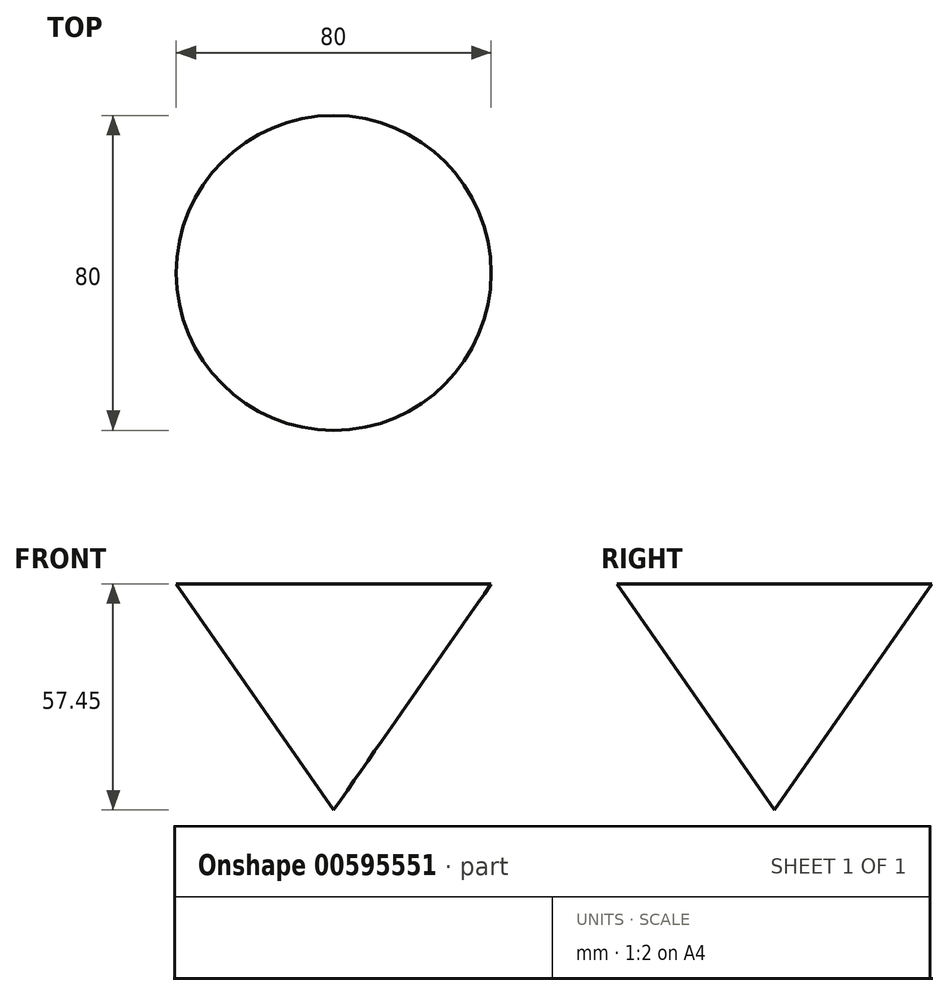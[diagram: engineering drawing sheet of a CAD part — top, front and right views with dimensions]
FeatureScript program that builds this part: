
annotation { "Feature Type Name" : "Feature", "Feature Type Description" : "" }
export const myFeature = defineFeature(function(context is Context, id is Id, definition is map)
    precondition{}
    {
        {
            var Q0;
            Q0=qCreatedBy(makeId("Front.planeOp"),FACE);
            var sketch = newSketch(context, id + "F0", { "sketchPlane" : qUnion([Q0])});
            skLineSegment(sketch, "E0", {"start": v(0, 0) * mm, "end": v(40, 57.45) * mm});
            skLineSegment(sketch, "E1", {"start": v(40, 57.45) * mm, "end": v(0, 57.45) * mm});
            skLineSegment(sketch, "E2", {"start": v(0, 57.45) * mm, "end": v(0, 0) * mm});
            skSolve(sketch);
        }
        {
            var Q0;
            Q0=makeQuery(id+"F0.imprint","IMPRINT",FACE,{"disambiguationData":[TD([[makeQuery(id+"F0.imprint","IMPRINT",EDGE,{"derivedFrom":sQuery(id+"F0.wireOp",EDGE,"E0")}),1.0]])]});
            var Q1;
            Q1=sQuery(id+"F0.wireOp",EDGE,"E2");
            revolve(context, id + "F1", {"entities" : qUnion([Q0]), "axis" : qUnion([Q1]), "revolveType" : RevolveType.FULL});
        }
    });
